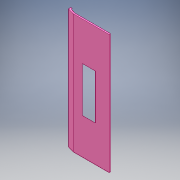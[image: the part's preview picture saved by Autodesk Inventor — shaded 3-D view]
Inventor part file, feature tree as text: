
AUTODESK INVENTOR PART (.ipt)
format: ipt  version: 2018 (Build 220112000, 112)  size: 164,352 bytes
history: native  units: mm
features: extrude x5, sketch x5, projected_geometry x1
ambient origin geometry x8: Origin, YZ Plane, XZ Plane, XY Plane, X Axis, Y Axis, Z Axis, Center Point
bodies: Solid1 (feature_tree)
feature tree (11):
  extrude  "Extrusion1"  Depth=560.0mm
  extrude  "Extrusion2"  Depth=1860.0mm TaperAngle=0.0deg
  extrude  "Extrusion3"  Depth=1.6mm
  extrude  "Extrusion4"  Depth=1.6mm TaperAngle=0.0deg
  extrude  "Extrusion5"  Depth=1.6mm
  sketch  "Sketch1"  dims[d0=560.0mm d2=100.0mm]
  sketch  "Sketch2"  dims[d3=37.0mm d5=1860.0mm d6=0.0mm]
  sketch  "Sketch3"  dims[d9=30.0mm d10=1.6mm]
  projected_geometry  "Projected Loop1"
  sketch  "Sketch4"  dims[d11=20.0mm d12=1.6mm d13=0.0mm]
  sketch  "Sketch5"  dims[d14=1.6mm d15=0.0mm d16=1.6mm d17=20.0mm d18=1.6mm d19=20.0mm d20=1160.0mm d21=0.0mm d22=200.0mm d23=700.0mm d24=560.0mm d25=10.0mm d26=0.0mm]
